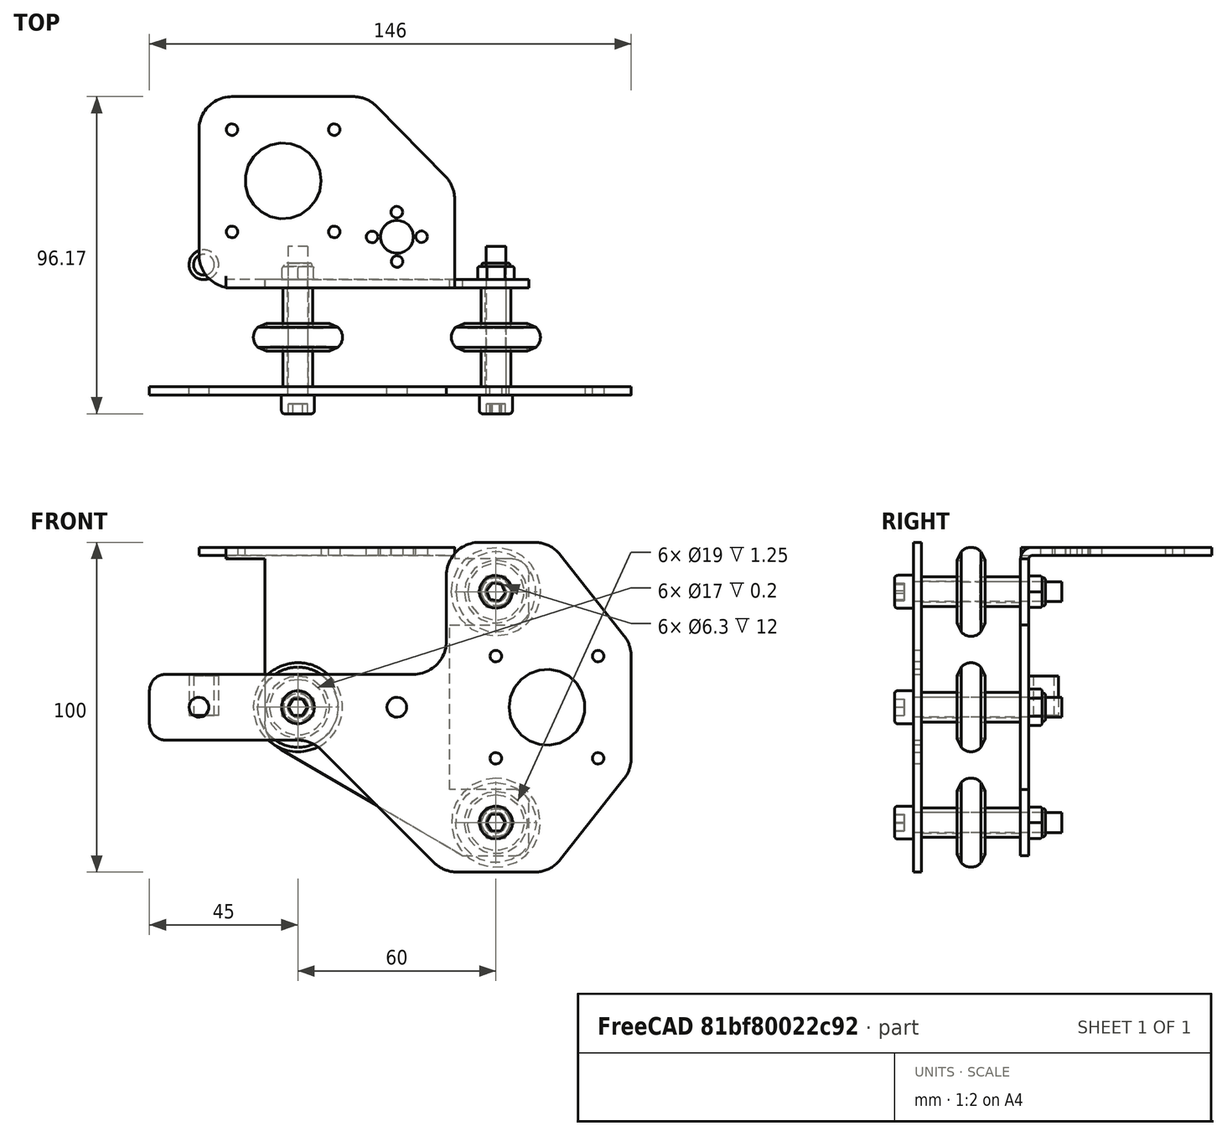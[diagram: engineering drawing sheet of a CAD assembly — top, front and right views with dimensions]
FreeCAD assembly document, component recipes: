
FREECAD ASSEMBLY — COMPONENT RECIPES ("TESTE")

This assembly document has 3 components, labeled P0..P2 below (a component is one placed body or linked part). 2 of them carry a construction recipe — the FreeCAD feature program that regenerates the part from scratch, quoted from this document or its linked companion documents; the rest are supplied as boundary geometry only. No exploded tour is included for this assembly.
COMPONENT P0 — recipe-attached ("Spacer001", modeled in this document).
Construction recipe (the document's own serialized feature program — sketch geometry with constraints, then the solid features built on it; lengths are millimeters unless a unit is written):

FEATURE [Sketcher::SketchObject] Sketch
  FullyConstrained = true
  MapMode = 5
  Support = -> [XY_Plane]
  sketch-geometry (2):
    g0: Circle CenterX=0 CenterY=0 CenterZ=0 NormalX=0 NormalY=0 NormalZ=1 AngleXU=0 Radius=3.15
    g1: Circle CenterX=0 CenterY=0 CenterZ=0 NormalX=0 NormalY=0 NormalZ=1 AngleXU=0 Radius=4.5
  constraints (4):
    c: Coincident(g0,g-1)
    c: Coincident(g1,g0)
    c: Diameter(g0) = 6.3
    c: Diameter(g1) = 9
FEATURE [PartDesign::Pad] Pad
  Direction = (1,1,1)
  Length = 12
  Length2 = 100
  Profile = -> Sketch
  Type = 0
FEATURE [PartDesign::Body] Body  label="Spacer"
  Group = -> [Sketch,Pad]
  Origin = -> Origin
  Tip = -> Pad
COMPONENT P1 — same part as P0; its construction recipe is shown at P0.
COMPONENT P2 — geometry summary ("Spacer006"; no construction recipe available for this part):
  bounding box: 12.0 x 9.0 x 9.0 mm
  tessellated surface: 1,008 triangles
  volume: 389 mm^3 (40% of its bounding box)
  symmetry: 2-fold rotationally symmetric about the x axis; 6-fold rotationally symmetric about the y axis; 2-fold rotationally symmetric about the z axis; mirror-symmetric across its x mid-plane, y mid-plane
PROVENANCE & LICENSES
A FreeCAD (.FCStd) document from a public repository crawl; recipes are the document's own serialized feature recipes (and, for linked parts, companion documents' recipes).
License: gpl-3.0.
